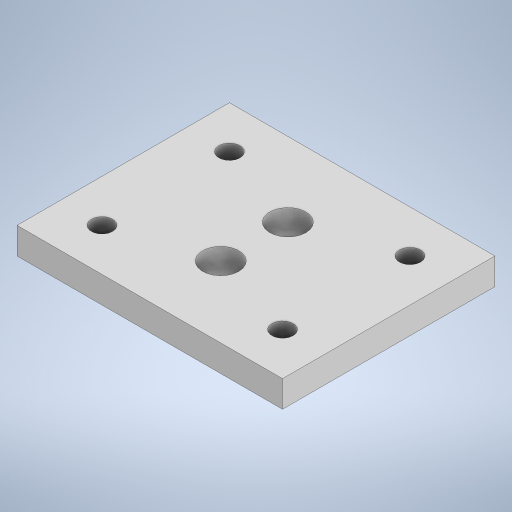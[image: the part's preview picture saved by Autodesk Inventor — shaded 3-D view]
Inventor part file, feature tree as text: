
AUTODESK INVENTOR PART (.ipt)
format: ipt  version: 2024.2 (Build 282272000, 272)  size: 241,664 bytes
history: native  units: in
note: dims shown in document units (in); Inventor stores cm internally (conversion verified against a paired STEP export)
features: extrude x2, sketch x2
ambient origin geometry x8: Origin, YZ Plane, XZ Plane, XY Plane, X Axis, Y Axis, Z Axis, Center Point
bodies: Solid1 (feature_tree)
feature tree (4):
  extrude  "Extrusion1"  Depth=1.0in
  extrude  "Extrusion2"  Depth=0.125in
  sketch  "Sketch1"  dims[d0=1.25in d1=1.0in]
  sketch  "Sketch2"  dims[d2=0.1in d3=0.1in d4=0.1in d5=0.1in d6=0.6in d7=0.85in d8=0.0in d9=0.0in d10=0.0in d11=0.0in d12=0.2in d13=0.2in d14=0.125in d15=0.0in d16=0.17in d17=0.35in d18=0.17in d19=0.316in d20=0.625in d21=0.625in d22=0.0in d23=0.0in]
